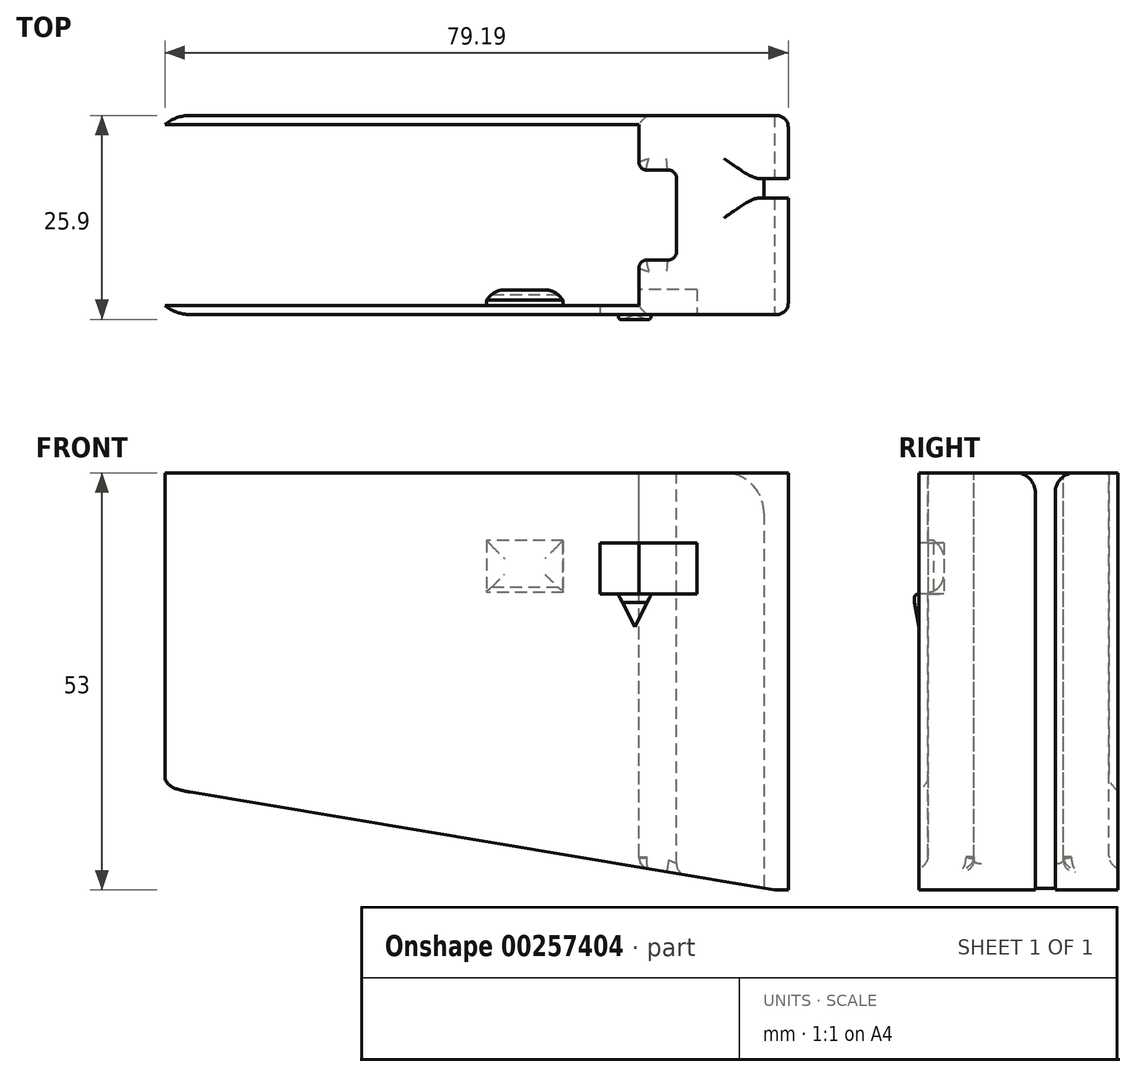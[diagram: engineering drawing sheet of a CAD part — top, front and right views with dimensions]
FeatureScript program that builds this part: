
annotation { "Feature Type Name" : "Feature", "Feature Type Description" : "" }
export const myFeature = defineFeature(function(context is Context, id is Id, definition is map)
    precondition{}
    {
        {
            var Q0;
            Q0=qCreatedBy(makeId("Top.planeOp"),FACE);
            var sketch = newSketch(context, id + "F0", { "sketchPlane" : qUnion([Q0])});
            skLineSegment(sketch, "E0.bottom", {"start": v(39, -12.65) * mm, "end": v(-35.5, -12.65) * mm});
            skLineSegment(sketch, "E0.top", {"start": v(39, 12.65) * mm, "end": v(-35.5, 12.65) * mm});
            skLineSegment(sketch, "E0.left", {"start": v(40.5, -11.15) * mm, "end": v(40.5, 2.15) * mm});
            skLineSegment(sketch, "E0.right", {"start": v(-40.5, -7.65) * mm, "end": v(-40.5, 7.65) * mm});
            skPoint(sketch, "E0.middle", {"position": v(0, 0) * mm});
            skPoint(sketch, "E1.visualSharp", {"position": v(-40.5, 12.65) * mm});
            skArc(sketch, "E1.filletArc", {"start": v(-35.5, 12.65) * mm, "mid": v(-39.04, 11.19) * mm, "end": v(-40.5, 7.65) * mm});
            skPoint(sketch, "E2.visualSharp", {"position": v(-40.5, -12.65) * mm});
            skArc(sketch, "E2.filletArc", {"start": v(-40.5, -7.65) * mm, "mid": v(-39.04, -11.19) * mm, "end": v(-35.5, -12.65) * mm});
            skPoint(sketch, "E3.visualSharp", {"position": v(40.5, -12.65) * mm});
            skArc(sketch, "E3.filletArc", {"start": v(39, -12.65) * mm, "mid": v(40.06, -12.21) * mm, "end": v(40.5, -11.15) * mm});
            skPoint(sketch, "E4.visualSharp", {"position": v(40.5, 12.65) * mm});
            skArc(sketch, "E4.filletArc", {"start": v(40.5, 11.15) * mm, "mid": v(40.06, 12.21) * mm, "end": v(39, 12.65) * mm});
            skLineSegment(sketch, "E5", {"start": v(29.56, 4.65) * mm, "end": v(40.5, 4.65) * mm, "construction": true});
            skLineSegment(sketch, "E6", {"start": v(31.3, 2.15) * mm, "end": v(40.5, 2.15) * mm, "construction": true});
            skPoint(sketch, "E7.visualSharp", {"position": v(42.9, 4.65) * mm});
            skPoint(sketch, "E8.visualSharp", {"position": v(42.9, 2.15) * mm});
            skLineSegment(sketch, "E9", {"start": v(40.5, 4.65) * mm, "end": v(37.4, 4.65) * mm});
            skLineSegment(sketch, "E10", {"start": v(37.4, 4.65) * mm, "end": v(37.4, 2.15) * mm});
            skLineSegment(sketch, "E11", {"start": v(37.4, 2.15) * mm, "end": v(40.5, 2.15) * mm});
            skLineSegment(sketch, "E12", {"start": v(40.5, 11.15) * mm, "end": v(40.5, 4.65) * mm});
            skSolve(sketch);
        }
        {
            var Q0;
            Q0 = qSketchRegion(id + "F0", true);
            extrude(context, id + "F1", {"entities" : qUnion([Q0]), "depth" : 76.2 * mm});
        }
        {
            var Q0;
            Q0=makeQuery(id+"F1.opExtrude","SWEPT_FACE",FACE,{"disambiguationData":[OSD([sQuery(id+"F0.wireOp",EDGE,"E0.bottom")])]});
            var sketch = newSketch(context, id + "F2", { "sketchPlane" : qUnion([Q0])});
            skLineSegment(sketch, "E13", {"start": v(39, 76.2) * mm, "end": v(40.5, 76.2) * mm, "construction": true});
            skLineSegment(sketch, "E14", {"start": v(40.5, 67.3) * mm, "end": v(28.9, 67.3) * mm, "construction": true});
            skLineSegment(sketch, "E15", {"start": v(28.9, 67.3) * mm, "end": v(28.9, 60.8) * mm});
            skLineSegment(sketch, "E16", {"start": v(28.9, 60.8) * mm, "end": v(16.6, 60.8) * mm});
            skPoint(sketch, "E17.orphan", {"position": v(16.6, 67.3) * mm});
            skLineSegment(sketch, "E18", {"start": v(28.9, 67.3) * mm, "end": v(16.6, 67.3) * mm});
            skLineSegment(sketch, "E19", {"start": v(16.6, 67.3) * mm, "end": v(16.6, 60.8) * mm});
            skSolve(sketch);
        }
        {
            var Q0;
            Q0=makeQuery(id+"F2.imprint","IMPRINT",FACE,{"disambiguationData":[TD([[makeQuery(id+"F2.imprint","IMPRINT",EDGE,{"derivedFrom":sQuery(id+"F2.wireOp",EDGE,"E15")}),-1.0]])]});
            extrude(context, id + "F3", {"entities" : qUnion([Q0]), "operationType" : NewBodyOperationType.REMOVE, "oppositeDirection" : true, "depth" : 3.2 * mm});
        }
        {
            var Q0;
            Q0=makeQuery(id+"F1.opExtrude","SWEPT_FACE",FACE,{"disambiguationData":[OSD([sQuery(id+"F0.wireOp",EDGE,"E0.bottom")])]});
            var sketch = newSketch(context, id + "F4", { "sketchPlane" : qUnion([Q0])});
            skLineSegment(sketch, "E20", {"start": v(21, 60.8) * mm, "end": v(21, 56.6) * mm, "construction": true});
            skLineSegment(sketch, "E21", {"start": v(18.9, 60.8) * mm, "end": v(23.1, 60.8) * mm});
            skLineSegment(sketch, "E22", {"start": v(18.9, 60.8) * mm, "end": v(21, 56.6) * mm});
            skLineSegment(sketch, "E23", {"start": v(21, 56.6) * mm, "end": v(23.1, 60.8) * mm});
            skSolve(sketch);
        }
        {
            var Q0;
            Q0=makeQuery(id+"F4.imprint","IMPRINT",FACE,{"disambiguationData":[TD([[makeQuery(id+"F4.imprint","IMPRINT",EDGE,{"derivedFrom":sQuery(id+"F4.wireOp",EDGE,"E21")}),1.0]])]});
            extrude(context, id + "F5", {"entities" : qUnion([Q0]), "operationType" : NewBodyOperationType.ADD, "depth" : 0.6 * mm});
        }
        {
            var Q0;
            Q0=makeQuery(id+"F5.opExtrude","CAP_EDGE",EDGE,{"disambiguationData":[OSD([sQuery(id+"F4.wireOp",EDGE,"E21")])],"isStart":false});
            fillet(context, id + "F6", {"entities" : qUnion([Q0]), "radius" : 0.5 * mm, "tangentPropagation" : true, "allowEdgeOverflow" : false});
        }
        {
            var Q0;
            Q0=makeQuery(id+"F3.boolean.opBoolean","COPY",FACE,{"derivedFrom":makeQuery(id+"F3.opExtrude","SWEPT_FACE",FACE,{"disambiguationData":[OSD([sQuery(id+"F2.wireOp",EDGE,"E19")])]})});
            cPlane(context, id + "F7", {"entities" : qUnion([Q0]), "cplaneType" : CPlaneType.OFFSET, "offset" : 8.9 * mm, "width" : 152.4 * mm, "height" : 152.4 * mm});
        }
        {
            var Q0;
            Q0=qCreatedBy(id+"F7.planeOp",FACE);
            var sketch = newSketch(context, id + "F8", { "sketchPlane" : qUnion([Q0])});
            skLineSegment(sketch, "E24", {"start": v(-13.33, 60.12) * mm, "end": v(-12.66, 56.6) * mm});
            skLineSegment(sketch, "E25", {"start": v(-12.66, 56.6) * mm, "end": v(-13.33, 56.6) * mm});
            skLineSegment(sketch, "E26", {"start": v(-13.33, 56.6) * mm, "end": v(-13.33, 60.12) * mm});
            skSolve(sketch);
        }
        {
            var Q0;
            Q0 = qSketchRegion(id + "F8", true);
            extrude(context, id + "F9", {"entities" : qUnion([Q0]), "operationType" : NewBodyOperationType.REMOVE, "endBound" : BoundingType.THROUGH_ALL, "oppositeDirection" : true, "depth" : 5.08 * mm});
        }
        {
            var Q0;
            Q0=qCreatedBy(makeId("Front.planeOp"),FACE);
            var sketch = newSketch(context, id + "F10", { "sketchPlane" : qUnion([Q0])});
            skLineSegment(sketch, "E27.top", {"start": v(-38.75, 0) * mm, "end": v(38.75, 0) * mm});
            skLineSegment(sketch, "E28", {"start": v(-38.75, 36.2) * mm, "end": v(38.75, 23.2) * mm});
            skLineSegment(sketch, "E29", {"start": v(-38.75, 36.2) * mm, "end": v(-38.75, 76.2) * mm, "construction": true});
            skLineSegment(sketch, "E30", {"start": v(-38.75, 76.2) * mm, "end": v(38.75, 76.2) * mm, "construction": true});
            skLineSegment(sketch, "E31", {"start": v(38.75, 76.2) * mm, "end": v(38.75, 23.2) * mm, "construction": true});
            skLineSegment(sketch, "E32", {"start": v(-38.75, 36.2) * mm, "end": v(-38.75, 0) * mm});
            skLineSegment(sketch, "E33", {"start": v(38.75, 0) * mm, "end": v(45.1, 0) * mm});
            skLineSegment(sketch, "E34", {"start": v(45.1, 0) * mm, "end": v(45.1, 23.2) * mm});
            skLineSegment(sketch, "E35", {"start": v(45.1, 23.2) * mm, "end": v(38.75, 23.2) * mm});
            skSolve(sketch);
        }
        {
            var Q0;
            Q0 = qSketchRegion(id + "F10", true);
            extrude(context, id + "F11", {"entities" : qUnion([Q0]), "operationType" : NewBodyOperationType.REMOVE, "endBound" : BoundingType.THROUGH_ALL, "oppositeDirection" : true, "depth" : 25.4 * mm, "hasSecondDirection" : true, "secondDirectionBound" : SecondDirectionBoundingType.THROUGH_ALL, "secondDirectionOppositeDirection" : false, "secondDirectionDepth" : 25.4 * mm});
        }
        {
            var Q0;
            Q0=makeQuery(id+"F1.opExtrude","CAP_FACE",FACE,{"disambiguationData":[OSD([sQuery(id+"F0.wireOp",EDGE,"E0.bottom"),sQuery(id+"F0.wireOp",EDGE,"E0.top"),sQuery(id+"F0.wireOp",EDGE,"E0.left"),sQuery(id+"F0.wireOp",EDGE,"E0.right"),sQuery(id+"F0.wireOp",EDGE,"E1.filletArc"),sQuery(id+"F0.wireOp",EDGE,"E2.filletArc"),sQuery(id+"F0.wireOp",EDGE,"E3.filletArc"),sQuery(id+"F0.wireOp",EDGE,"E4.filletArc"),sQuery(id+"F0.wireOp",EDGE,"9pMwYVjw-FA8m-ow9E-PsMu-IHw6mw6Qwgzp.bottom"),sQuery(id+"F0.wireOp",EDGE,"9pMwYVjw-FA8m-ow9E-PsMu-IHw6mw6Qwgzp.top"),sQuery(id+"F0.wireOp",EDGE,"9pMwYVjw-FA8m-ow9E-PsMu-IHw6mw6Qwgzp.right"),sQuery(id+"F0.wireOp",EDGE,"E7.filletArc"),sQuery(id+"F0.wireOp",EDGE,"E8.filletArc"),sQuery(id+"F0.wireOp",EDGE,"193429f0-9ee1-40c5-b7a5-fca97fa292dd.trimOffspring")])],"isStart":false});
            var sketch = newSketch(context, id + "F12", { "sketchPlane" : qUnion([Q0])});
            skLineSegment(sketch, "E36.bottom", {"start": v(21.55, -11.5) * mm, "end": v(-40.05, -11.5) * mm});
            skLineSegment(sketch, "E36.top", {"start": v(21.55, 11.5) * mm, "end": v(-40.05, 11.5) * mm});
            skLineSegment(sketch, "E36.left", {"start": v(21.55, -11.5) * mm, "end": v(21.55, -5.7) * mm});
            skLineSegment(sketch, "E36.right", {"start": v(-40.05, -11.5) * mm, "end": v(-40.05, 11.5) * mm});
            skPoint(sketch, "E36.middle", {"position": v(0, 0) * mm});
            skLineSegment(sketch, "E37", {"start": v(21.55, 0) * mm, "end": v(26.3, 0) * mm, "construction": true});
            skPoint(sketch, "E37.endSnap0", {"position": v(21.55, 0) * mm});
            skLineSegment(sketch, "E38", {"start": v(26.3, 0) * mm, "end": v(26.3, 5.7) * mm});
            skLineSegment(sketch, "E39", {"start": v(26.3, 5.7) * mm, "end": v(21.55, 5.7) * mm});
            skLineSegment(sketch, "E40.MirrorCS", {"start": v(26.3, 0) * mm, "end": v(26.3, -5.7) * mm});
            skLineSegment(sketch, "E41.MirrorCS", {"start": v(26.3, -5.7) * mm, "end": v(21.55, -5.7) * mm});
            skLineSegment(sketch, "E42.trimOffspring", {"start": v(21.55, 5.7) * mm, "end": v(21.55, 11.5) * mm});
            skLineSegment(sketch, "E43", {"start": v(-40.05, 11.5) * mm, "end": v(-46.12, 11.5) * mm});
            skLineSegment(sketch, "E44", {"start": v(-46.12, 11.5) * mm, "end": v(-46.12, -11.5) * mm});
            skLineSegment(sketch, "E45", {"start": v(-46.12, -11.5) * mm, "end": v(-40.05, -11.5) * mm});
            skSolve(sketch);
        }
        {
            var Q0;
            Q0 = qSketchRegion(id + "F12", true);
            extrude(context, id + "F13", {"entities" : qUnion([Q0]), "operationType" : NewBodyOperationType.REMOVE, "endBound" : BoundingType.THROUGH_ALL, "oppositeDirection" : true, "depth" : 25.4 * mm});
        }
        {
            var Q0;
            Q0=makeQuery(id+"F13.boolean.opBoolean","COPY",EDGE,{"derivedFrom":makeQuery(id+"F13.opExtrude","SWEPT_EDGE",EDGE,{"disambiguationData":[OSD([sQuery(id+"F12.wireOp",EDGE,"E36.left"),sQuery(id+"F12.wireOp",EDGE,"E41.MirrorCS")])]})});
            var Q1;
            Q1=makeQuery(id+"F13.boolean.opBoolean","COPY",EDGE,{"derivedFrom":makeQuery(id+"F13.opExtrude","SWEPT_EDGE",EDGE,{"disambiguationData":[OSD([sQuery(id+"F12.wireOp",EDGE,"E40.MirrorCS"),sQuery(id+"F12.wireOp",EDGE,"E41.MirrorCS")])]})});
            var Q2;
            Q2=makeQuery(id+"F13.boolean.opBoolean","COPY",EDGE,{"derivedFrom":makeQuery(id+"F13.opExtrude","SWEPT_EDGE",EDGE,{"disambiguationData":[OSD([sQuery(id+"F12.wireOp",EDGE,"E39"),sQuery(id+"F12.wireOp",EDGE,"E42.trimOffspring")])]})});
            var Q3;
            Q3=makeQuery(id+"F13.boolean.opBoolean","COPY",EDGE,{"derivedFrom":makeQuery(id+"F13.opExtrude","SWEPT_EDGE",EDGE,{"disambiguationData":[OSD([sQuery(id+"F12.wireOp",EDGE,"E38"),sQuery(id+"F12.wireOp",EDGE,"E39")])]})});
            fillet(context, id + "F14", {"entities" : qUnion([Q0, Q1, Q2, Q3]), "radius" : 1 * mm, "tangentPropagation" : true, "allowEdgeOverflow" : false});
        }
        {
            var Q0;
            Q0=makeQuery(id+"F13.boolean.opBoolean","COPY",FACE,{"derivedFrom":makeQuery(id+"F13.opExtrude","SWEPT_FACE",FACE,{"disambiguationData":[OSD([sQuery(id+"F12.wireOp",EDGE,"E36.bottom")])]})});
            var sketch = newSketch(context, id + "F15", { "sketchPlane" : qUnion([Q0])});
            skLineSegment(sketch, "E46.bottom", {"start": v(-11.9, 67.6) * mm, "end": v(-2.15, 67.6) * mm});
            skLineSegment(sketch, "E46.top", {"start": v(-11.9, 61) * mm, "end": v(-2.15, 61) * mm});
            skLineSegment(sketch, "E46.left", {"start": v(-11.9, 67.6) * mm, "end": v(-11.9, 61) * mm});
            skLineSegment(sketch, "E46.right", {"start": v(-2.15, 67.6) * mm, "end": v(-2.15, 61) * mm});
            skSolve(sketch);
        }
        {
            var Q0;
            Q0 = qSketchRegion(id + "F15", true);
            extrude(context, id + "F16", {"entities" : qUnion([Q0]), "operationType" : NewBodyOperationType.ADD, "depth" : 2 * mm});
        }
        {
            var Q0;
            Q0=makeQuery(id+"F16.opExtrude","CAP_EDGE",EDGE,{"disambiguationData":[OSD([sQuery(id+"F15.wireOp",EDGE,"E46.bottom")])],"isStart":false});
            var Q1;
            Q1=makeQuery(id+"F16.opExtrude","CAP_EDGE",EDGE,{"disambiguationData":[OSD([sQuery(id+"F15.wireOp",EDGE,"E46.right")])],"isStart":false});
            var Q2;
            Q2=makeQuery(id+"F16.opExtrude","CAP_EDGE",EDGE,{"disambiguationData":[OSD([sQuery(id+"F15.wireOp",EDGE,"E46.left")])],"isStart":false});
            var Q3;
            Q3=makeQuery(id+"F16.opExtrude","CAP_EDGE",EDGE,{"disambiguationData":[OSD([sQuery(id+"F15.wireOp",EDGE,"E46.top")])],"isStart":false});
            chamfer(context, id + "F17", {"entities" : qUnion([Q0, Q1, Q2, Q3]), "width" : 1.27 * mm, "tangentPropagation" : true});
        }
        {
            var Q0;
            {var subQ0=sQuery(id+"F15.wireOp",EDGE,"E46.bottom");Q0=makeQuery(id+"F17.opChamfer","BLEND_EDGE",EDGE,{"blendedFrom":[makeQuery(id+"F16.opExtrude","CAP_EDGE",EDGE,{"disambiguationData":[OSD([subQ0])],"isStart":false}),makeQuery(id+"F16.opExtrude","CAP_FACE",FACE,{"disambiguationData":[OSD([subQ0,sQuery(id+"F15.wireOp",EDGE,"E46.top"),sQuery(id+"F15.wireOp",EDGE,"E46.left"),sQuery(id+"F15.wireOp",EDGE,"E46.right")])],"isStart":false})],"blendedInto":[makeQuery(id+"F16.opExtrude","CAP_FACE",FACE,{"disambiguationData":[OSD([subQ0,sQuery(id+"F15.wireOp",EDGE,"E46.top"),sQuery(id+"F15.wireOp",EDGE,"E46.left"),sQuery(id+"F15.wireOp",EDGE,"E46.right")])],"isStart":false})]});}
            var Q1;
            {var subQ0=sQuery(id+"F15.wireOp",EDGE,"E46.right");Q1=makeQuery(id+"F17.opChamfer","BLEND_EDGE",EDGE,{"blendedFrom":[makeQuery(id+"F16.opExtrude","CAP_EDGE",EDGE,{"disambiguationData":[OSD([subQ0])],"isStart":false}),makeQuery(id+"F16.opExtrude","CAP_FACE",FACE,{"disambiguationData":[OSD([sQuery(id+"F15.wireOp",EDGE,"E46.bottom"),sQuery(id+"F15.wireOp",EDGE,"E46.top"),sQuery(id+"F15.wireOp",EDGE,"E46.left"),subQ0])],"isStart":false})],"blendedInto":[makeQuery(id+"F16.opExtrude","CAP_FACE",FACE,{"disambiguationData":[OSD([sQuery(id+"F15.wireOp",EDGE,"E46.bottom"),sQuery(id+"F15.wireOp",EDGE,"E46.top"),sQuery(id+"F15.wireOp",EDGE,"E46.left"),subQ0])],"isStart":false})]});}
            var Q2;
            {var subQ0=sQuery(id+"F15.wireOp",EDGE,"E46.top");Q2=makeQuery(id+"F17.opChamfer","BLEND_EDGE",EDGE,{"blendedFrom":[makeQuery(id+"F16.opExtrude","CAP_EDGE",EDGE,{"disambiguationData":[OSD([subQ0])],"isStart":false}),makeQuery(id+"F16.opExtrude","CAP_FACE",FACE,{"disambiguationData":[OSD([sQuery(id+"F15.wireOp",EDGE,"E46.bottom"),subQ0,sQuery(id+"F15.wireOp",EDGE,"E46.left"),sQuery(id+"F15.wireOp",EDGE,"E46.right")])],"isStart":false})],"blendedInto":[makeQuery(id+"F16.opExtrude","CAP_FACE",FACE,{"disambiguationData":[OSD([sQuery(id+"F15.wireOp",EDGE,"E46.bottom"),subQ0,sQuery(id+"F15.wireOp",EDGE,"E46.left"),sQuery(id+"F15.wireOp",EDGE,"E46.right")])],"isStart":false})]});}
            var Q3;
            {var subQ0=sQuery(id+"F15.wireOp",EDGE,"E46.left");Q3=makeQuery(id+"F17.opChamfer","BLEND_EDGE",EDGE,{"blendedFrom":[makeQuery(id+"F16.opExtrude","CAP_EDGE",EDGE,{"disambiguationData":[OSD([subQ0])],"isStart":false}),makeQuery(id+"F16.opExtrude","CAP_FACE",FACE,{"disambiguationData":[OSD([sQuery(id+"F15.wireOp",EDGE,"E46.bottom"),sQuery(id+"F15.wireOp",EDGE,"E46.top"),subQ0,sQuery(id+"F15.wireOp",EDGE,"E46.right")])],"isStart":false})],"blendedInto":[makeQuery(id+"F16.opExtrude","CAP_FACE",FACE,{"disambiguationData":[OSD([sQuery(id+"F15.wireOp",EDGE,"E46.bottom"),sQuery(id+"F15.wireOp",EDGE,"E46.top"),subQ0,sQuery(id+"F15.wireOp",EDGE,"E46.right")])],"isStart":false})]});}
            fillet(context, id + "F18", {"entities" : qUnion([Q0, Q1, Q2, Q3]), "radius" : 2.54 * mm, "tangentPropagation" : true, "allowEdgeOverflow" : false});
        }
        {
            var Q0;
            Q0=makeQuery(id+"F11.boolean.opBoolean","COPY",FACE,{"derivedFrom":makeQuery(id+"F11.opExtrude","SWEPT_FACE",FACE,{"disambiguationData":[OSD([sQuery(id+"F10.wireOp",EDGE,"E28")])]})});
            var sketch = newSketch(context, id + "F19", { "sketchPlane" : qUnion([Q0])});
            skLineSegment(sketch, "E47.left", {"start": v(14.93, -11.48) * mm, "end": v(14.93, -6.68) * mm});
            skLineSegment(sketch, "E48", {"start": v(14.93, 0.02) * mm, "end": v(19.68, 0.02) * mm, "construction": true});
            skPoint(sketch, "E48.endSnap0", {"position": v(14.93, 0.02) * mm});
            skLineSegment(sketch, "E49", {"start": v(19.68, 0.02) * mm, "end": v(19.68, 4.72) * mm});
            skLineSegment(sketch, "E50", {"start": v(18.68, 5.72) * mm, "end": v(15.93, 5.72) * mm});
            skLineSegment(sketch, "E51.MirrorCS", {"start": v(19.68, 0.02) * mm, "end": v(19.68, -4.68) * mm});
            skLineSegment(sketch, "E52.MirrorCS", {"start": v(18.68, -5.68) * mm, "end": v(15.93, -5.68) * mm});
            skLineSegment(sketch, "E53.trimOffspring", {"start": v(14.93, 6.72) * mm, "end": v(14.93, 11.52) * mm});
            skLineSegment(sketch, "E54", {"start": v(14.93, 11.52) * mm, "end": v(23.57, 11.52) * mm});
            skLineSegment(sketch, "E55", {"start": v(23.57, 11.52) * mm, "end": v(23.57, -11.5) * mm});
            skLineSegment(sketch, "E56", {"start": v(23.57, -11.5) * mm, "end": v(14.93, -11.48) * mm});
            skPoint(sketch, "E57.visualSharp", {"position": v(14.93, -5.68) * mm});
            skArc(sketch, "E57.filletArc", {"start": v(15.93, -5.68) * mm, "mid": v(15.22, -5.98) * mm, "end": v(14.93, -6.68) * mm});
            skPoint(sketch, "E58.visualSharp", {"position": v(19.68, -5.68) * mm});
            skArc(sketch, "E58.filletArc", {"start": v(18.68, -5.68) * mm, "mid": v(19.39, -5.39) * mm, "end": v(19.68, -4.68) * mm});
            skPoint(sketch, "E59.visualSharp", {"position": v(19.68, 5.72) * mm});
            skArc(sketch, "E59.filletArc", {"start": v(19.68, 4.72) * mm, "mid": v(19.39, 5.42) * mm, "end": v(18.68, 5.72) * mm});
            skPoint(sketch, "E60.visualSharp", {"position": v(14.93, 5.72) * mm});
            skArc(sketch, "E60.filletArc", {"start": v(14.93, 6.72) * mm, "mid": v(15.22, 6.01) * mm, "end": v(15.93, 5.72) * mm});
            skSolve(sketch);
        }
        {
            var Q0;
            Q0=makeQuery(id+"F1.opExtrude","CAP_FACE",FACE,{"disambiguationData":[OSD([sQuery(id+"F0.wireOp",EDGE,"E0.bottom"),sQuery(id+"F0.wireOp",EDGE,"E0.top"),sQuery(id+"F0.wireOp",EDGE,"E0.left"),sQuery(id+"F0.wireOp",EDGE,"E0.right"),sQuery(id+"F0.wireOp",EDGE,"E1.filletArc"),sQuery(id+"F0.wireOp",EDGE,"E2.filletArc"),sQuery(id+"F0.wireOp",EDGE,"E3.filletArc"),sQuery(id+"F0.wireOp",EDGE,"E4.filletArc"),sQuery(id+"F0.wireOp",EDGE,"E9"),sQuery(id+"F0.wireOp",EDGE,"E10"),sQuery(id+"F0.wireOp",EDGE,"E11"),sQuery(id+"F0.wireOp",EDGE,"E12")])],"isStart":false});
            var sketch = newSketch(context, id + "F20", { "sketchPlane" : qUnion([Q0])});
            skLineSegment(sketch, "E61", {"start": v(19.96, 0) * mm, "end": v(24.71, 0) * mm, "construction": true});
            skPoint(sketch, "E61.endSnap0", {"position": v(19.96, 0) * mm});
            skLineSegment(sketch, "E62", {"start": v(24.71, 0) * mm, "end": v(24.71, 4.7) * mm});
            skLineSegment(sketch, "E63", {"start": v(23.71, 5.7) * mm, "end": v(22.56, 5.7) * mm});
            skLineSegment(sketch, "E64.MirrorCS", {"start": v(24.71, 0) * mm, "end": v(24.71, -4.7) * mm});
            skLineSegment(sketch, "E65.MirrorCS", {"start": v(23.71, -5.7) * mm, "end": v(22.56, -5.7) * mm});
            skLineSegment(sketch, "E66", {"start": v(28.56, 11.5) * mm, "end": v(28.56, -11.5) * mm});
            skPoint(sketch, "E67.visualSharp", {"position": v(19.96, 5.7) * mm});
            skArc(sketch, "E67.filletArc", {"start": v(21.56, 6.7) * mm, "mid": v(21.86, 6) * mm, "end": v(22.56, 5.7) * mm});
            skPoint(sketch, "E68.visualSharp", {"position": v(24.71, 5.7) * mm});
            skArc(sketch, "E68.filletArc", {"start": v(24.71, 4.7) * mm, "mid": v(24.42, 5.4) * mm, "end": v(23.71, 5.7) * mm});
            skPoint(sketch, "E69.visualSharp", {"position": v(24.71, -5.7) * mm});
            skArc(sketch, "E69.filletArc", {"start": v(23.71, -5.7) * mm, "mid": v(24.42, -5.4) * mm, "end": v(24.71, -4.7) * mm});
            skPoint(sketch, "E70.visualSharp", {"position": v(19.96, -5.7) * mm});
            skArc(sketch, "E70.filletArc", {"start": v(22.56, -5.7) * mm, "mid": v(21.86, -6) * mm, "end": v(21.56, -6.7) * mm});
            skLineSegment(sketch, "E71", {"start": v(28.56, 11.5) * mm, "end": v(21.55, 11.5) * mm});
            skLineSegment(sketch, "E72", {"start": v(21.55, 11.5) * mm, "end": v(21.56, 6.7) * mm});
            skLineSegment(sketch, "E73", {"start": v(21.56, -6.7) * mm, "end": v(21.55, -11.5) * mm});
            skLineSegment(sketch, "E74", {"start": v(21.55, -11.5) * mm, "end": v(28.56, -11.5) * mm});
            skSolve(sketch);
        }
        {
            var Q0;
            Q0=makeQuery(id+"F13.boolean.opBoolean","INTERSECT",EDGE,{"derivedFrom":[makeQuery(id+"F11.boolean.opBoolean","COPY",FACE,{"derivedFrom":makeQuery(id+"F11.opExtrude","SWEPT_FACE",FACE,{"disambiguationData":[OSD([sQuery(id+"F10.wireOp",EDGE,"E28")])]})}),makeQuery(id+"F13.opExtrude","SWEPT_FACE",FACE,{"disambiguationData":[OSD([sQuery(id+"F12.wireOp",EDGE,"E36.bottom"),sQuery(id+"F12.wireOp",EDGE,"E45")])]})]});
            var Q1;
            Q1=makeQuery(id+"F13.boolean.opBoolean","INTERSECT",EDGE,{"derivedFrom":[makeQuery(id+"F11.boolean.opBoolean","COPY",FACE,{"derivedFrom":makeQuery(id+"F11.opExtrude","SWEPT_FACE",FACE,{"disambiguationData":[OSD([sQuery(id+"F10.wireOp",EDGE,"E28")])]})}),makeQuery(id+"F13.opExtrude","SWEPT_FACE",FACE,{"disambiguationData":[OSD([sQuery(id+"F12.wireOp",EDGE,"E36.top"),sQuery(id+"F12.wireOp",EDGE,"E43")])]})]});
            var Q2;
            Q2=makeQuery(id+"F13.boolean.opBoolean","INTERSECT",EDGE,{"derivedFrom":[makeQuery(id+"F11.boolean.opBoolean","COPY",FACE,{"derivedFrom":makeQuery(id+"F11.opExtrude","SWEPT_FACE",FACE,{"disambiguationData":[OSD([sQuery(id+"F10.wireOp",EDGE,"E28")])]})}),makeQuery(id+"F13.opExtrude","SWEPT_FACE",FACE,{"disambiguationData":[OSD([sQuery(id+"F12.wireOp",EDGE,"E42.trimOffspring")])]})]});
            fillet(context, id + "F21", {"entities" : qUnion([Q0, Q1, Q2]), "radius" : 1.5 * mm, "tangentPropagation" : true, "allowEdgeOverflow" : false});
        }
        {
            var Q0;
            Q0=makeQuery(id+"F1.opExtrude","CAP_EDGE",EDGE,{"disambiguationData":[OSD([sQuery(id+"F0.wireOp",EDGE,"E9")])],"isStart":false});
            var Q1;
            Q1=makeQuery(id+"F1.opExtrude","CAP_EDGE",EDGE,{"disambiguationData":[OSD([sQuery(id+"F0.wireOp",EDGE,"E11")])],"isStart":false});
            fillet(context, id + "F22", {"entities" : qUnion([Q0, Q1]), "radius" : 2.54 * mm, "tangentPropagation" : true, "allowEdgeOverflow" : false});
        }
        {
            var Q0;
            Q0=makeQuery(id+"F1.opExtrude","CAP_EDGE",EDGE,{"disambiguationData":[OSD([sQuery(id+"F0.wireOp",EDGE,"E10")])],"isStart":false});
            fillet(context, id + "F23", {"entities" : qUnion([Q0]), "radius" : 5.08 * mm, "tangentPropagation" : true, "allowEdgeOverflow" : false});
        }
        {
            var Q0;
            {var subQ0=sQuery(id+"F15.wireOp",EDGE,"E46.top");Q0=makeQuery(id+"F17.opChamfer","BLEND_EDGE",EDGE,{"blendedFrom":[makeQuery(id+"F16.opExtrude","CAP_EDGE",EDGE,{"disambiguationData":[OSD([subQ0])],"isStart":false}),makeQuery(id+"F16.opExtrude","SWEPT_FACE",FACE,{"disambiguationData":[OSD([subQ0])]})],"blendedInto":[makeQuery(id+"F16.opExtrude","SWEPT_FACE",FACE,{"disambiguationData":[OSD([subQ0])]})]});}
            fillet(context, id + "F24", {"entities" : qUnion([Q0]), "radius" : 2.54 * mm, "tangentPropagation" : true, "allowEdgeOverflow" : false});
        }
    });
